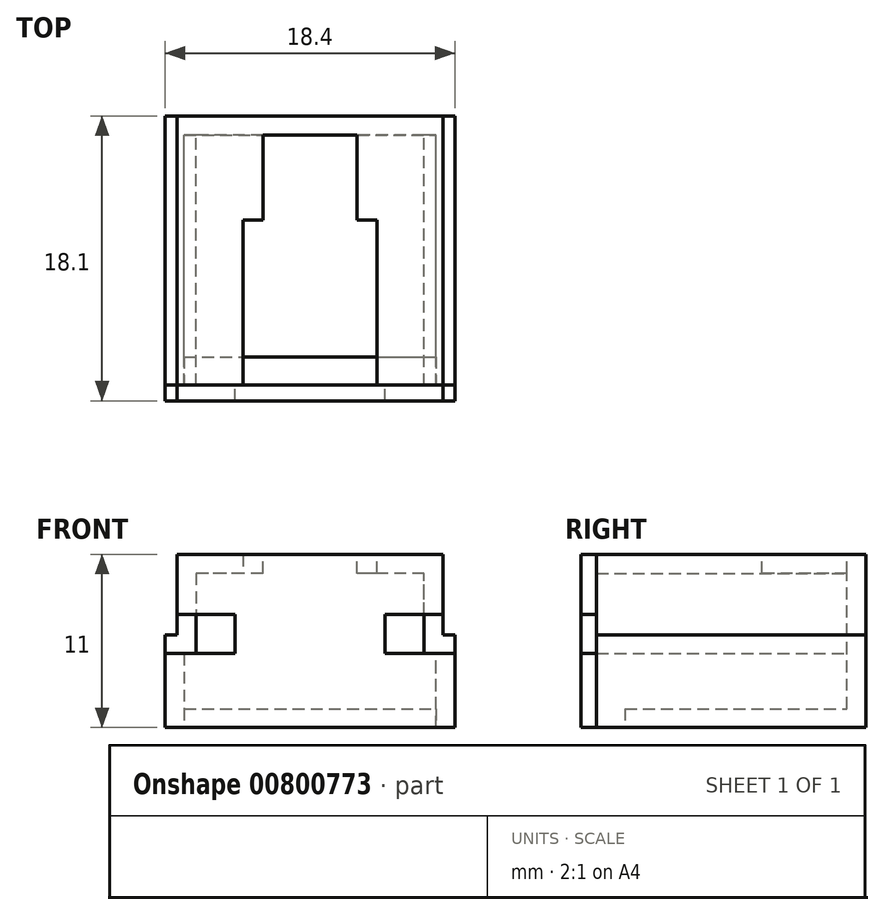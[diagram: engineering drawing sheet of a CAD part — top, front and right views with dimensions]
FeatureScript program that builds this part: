
annotation { "Feature Type Name" : "Feature", "Feature Type Description" : "" }
export const myFeature = defineFeature(function(context is Context, id is Id, definition is map)
    precondition{}
    {
        {
            var Q0;
            Q0=qCreatedBy(makeId("Front.planeOp"),FACE);
            var sketch = newSketch(context, id + "F0", { "sketchPlane" : qUnion([Q0])});
            skLineSegment(sketch, "E0", {"start": v(-9.2, 0) * mm, "end": v(9.2, 0) * mm});
            skLineSegment(sketch, "E1", {"start": v(-8.45, 11) * mm, "end": v(-4.25, 11) * mm});
            skLineSegment(sketch, "E2", {"start": v(-4.25, 11) * mm, "end": v(-4.25, 9.8) * mm});
            skLineSegment(sketch, "E3", {"start": v(-4.25, 9.8) * mm, "end": v(-7.25, 9.8) * mm});
            skLineSegment(sketch, "E4", {"start": v(-7.25, 9.8) * mm, "end": v(-7.25, 4.7) * mm});
            skLineSegment(sketch, "E5", {"start": v(-7.25, 4.7) * mm, "end": v(-8, 4.7) * mm});
            skLineSegment(sketch, "E6", {"start": v(-8, 4.7) * mm, "end": v(-8, 1.2) * mm});
            skLineSegment(sketch, "E7", {"start": v(-8, 1.2) * mm, "end": v(8, 1.2) * mm});
            skLineSegment(sketch, "E8", {"start": v(8, 1.2) * mm, "end": v(8, 4.7) * mm});
            skLineSegment(sketch, "E9", {"start": v(8, 4.7) * mm, "end": v(7.25, 4.7) * mm});
            skLineSegment(sketch, "E10", {"start": v(7.25, 4.7) * mm, "end": v(7.25, 9.8) * mm});
            skLineSegment(sketch, "E11", {"start": v(7.25, 9.8) * mm, "end": v(4.25, 9.8) * mm});
            skLineSegment(sketch, "E12", {"start": v(4.25, 9.8) * mm, "end": v(4.25, 11) * mm});
            skLineSegment(sketch, "E13", {"start": v(4.25, 11) * mm, "end": v(8.45, 11) * mm});
            skLineSegment(sketch, "E14", {"start": v(4.25, 11) * mm, "end": v(-4.25, 11) * mm, "construction": true});
            skLineSegment(sketch, "E15", {"start": v(0, 0) * mm, "end": v(0, 11) * mm, "construction": true});
            skLineSegment(sketch, "E16.bottom", {"start": v(4.25, 9.8) * mm, "end": v(3, 9.8) * mm});
            skLineSegment(sketch, "E16.top", {"start": v(4.25, 11) * mm, "end": v(3, 11) * mm});
            skLineSegment(sketch, "E16.right", {"start": v(3, 9.8) * mm, "end": v(3, 11) * mm});
            skLineSegment(sketch, "E17.bottom", {"start": v(-4.25, 9.8) * mm, "end": v(-3, 9.8) * mm});
            skLineSegment(sketch, "E17.top", {"start": v(-4.25, 11) * mm, "end": v(-3, 11) * mm});
            skLineSegment(sketch, "E17.left", {"start": v(-4.25, 9.8) * mm, "end": v(-4.25, 11) * mm});
            skLineSegment(sketch, "E17.right", {"start": v(-3, 9.8) * mm, "end": v(-3, 11) * mm});
            skLineSegment(sketch, "E18", {"start": v(-9.2, 0) * mm, "end": v(-9.2, 5.9) * mm});
            skLineSegment(sketch, "E19", {"start": v(-9.2, 5.9) * mm, "end": v(-8.45, 5.9) * mm});
            skLineSegment(sketch, "E20", {"start": v(-8.45, 5.9) * mm, "end": v(-8.45, 11) * mm});
            skLineSegment(sketch, "E21", {"start": v(9.2, 0) * mm, "end": v(9.2, 5.9) * mm});
            skLineSegment(sketch, "E22", {"start": v(9.2, 5.9) * mm, "end": v(8.45, 5.9) * mm});
            skLineSegment(sketch, "E23", {"start": v(8.45, 5.9) * mm, "end": v(8.45, 11) * mm});
            skSolve(sketch);
        }
        {
            var Q0;
            Q0=makeQuery(id+"F0.imprint","IMPRINT",FACE,{"disambiguationData":[TD([[makeQuery(id+"F0.imprint","IMPRINT",EDGE,{"derivedFrom":sQuery(id+"F0.wireOp",EDGE,"E0")}),1.0]])]});
            extrude(context, id + "F1", {"entities" : qUnion([Q0]), "depth" : 10.5 * mm, "offsetDistance" : 25 * mm});
        }
        {
            var Q0;
            Q0=makeQuery(id+"F0.imprint","IMPRINT",FACE,{"disambiguationData":[TD([[makeQuery(id+"F0.imprint","IMPRINT",EDGE,{"derivedFrom":sQuery(id+"F0.wireOp",EDGE,"E16.bottom")}),-1.0]])]});
            var Q1;
            Q1=makeQuery(id+"F0.imprint","IMPRINT",FACE,{"disambiguationData":[TD([[makeQuery(id+"F0.imprint","IMPRINT",EDGE,{"derivedFrom":sQuery(id+"F0.wireOp",EDGE,"E0")}),1.0]])]});
            var Q2;
            Q2=makeQuery(id+"F0.imprint","IMPRINT",FACE,{"disambiguationData":[TD([[makeQuery(id+"F0.imprint","IMPRINT",EDGE,{"derivedFrom":sQuery(id+"F0.wireOp",EDGE,"E17.bottom")}),1.0]])]});
            extrude(context, id + "F2", {"entities" : qUnion([Q0, Q1, Q2]), "operationType" : NewBodyOperationType.ADD, "oppositeDirection" : true, "depth" : 5.4 * mm, "offsetDistance" : 25 * mm});
        }
        {
            var Q0;
            Q0=makeQuery(id+"F2.opExtrude","CAP_FACE",FACE,{"disambiguationData":[OSD([sQuery(id+"F0.wireOp",EDGE,"E0"),sQuery(id+"F0.wireOp",EDGE,"EI1BiXlL-Q3jm-eNfy-wKam-WfHQaEUP30CD"),sQuery(id+"F0.wireOp",EDGE,"E1"),sQuery(id+"F0.wireOp",EDGE,"E3"),sQuery(id+"F0.wireOp",EDGE,"E4"),sQuery(id+"F0.wireOp",EDGE,"E5"),sQuery(id+"F0.wireOp",EDGE,"E6"),sQuery(id+"F0.wireOp",EDGE,"E7"),sQuery(id+"F0.wireOp",EDGE,"E8"),sQuery(id+"F0.wireOp",EDGE,"E9"),sQuery(id+"F0.wireOp",EDGE,"E10"),sQuery(id+"F0.wireOp",EDGE,"E11"),sQuery(id+"F0.wireOp",EDGE,"E13"),sQuery(id+"F0.wireOp",EDGE,"ufck05Tf-Zb9H-2oP1-nLNF-ijk2fNiCipJR"),sQuery(id+"F0.wireOp",EDGE,"E16.bottom"),sQuery(id+"F0.wireOp",EDGE,"E16.top"),sQuery(id+"F0.wireOp",EDGE,"E16.right"),sQuery(id+"F0.wireOp",EDGE,"E17.bottom"),sQuery(id+"F0.wireOp",EDGE,"E17.top"),sQuery(id+"F0.wireOp",EDGE,"E17.right")])],"isStart":false});
            var sketch = newSketch(context, id + "F3", { "sketchPlane" : qUnion([Q0])});
            skLineSegment(sketch, "E24.0.3", {"start": v(-8.45, 11) * mm, "end": v(-8.45, 5.9) * mm});
            skLineSegment(sketch, "E24.0.4", {"start": v(-8.45, 5.9) * mm, "end": v(-9.2, 5.9) * mm});
            skLineSegment(sketch, "E24.0.5", {"start": v(-9.2, 5.9) * mm, "end": v(-9.2, 0) * mm});
            skLineSegment(sketch, "E24.0.6", {"start": v(-9.2, 0) * mm, "end": v(9.2, 0) * mm});
            skLineSegment(sketch, "E24.0.7", {"start": v(9.2, 0) * mm, "end": v(9.2, 5.9) * mm});
            skLineSegment(sketch, "E24.0.8", {"start": v(9.2, 5.9) * mm, "end": v(8.45, 5.9) * mm});
            skLineSegment(sketch, "E24.0.9", {"start": v(8.45, 5.9) * mm, "end": v(8.45, 11) * mm});
            skLineSegment(sketch, "E25", {"start": v(-8.45, 11) * mm, "end": v(8.45, 11) * mm});
            skSolve(sketch);
        }
        {
            var Q0;
            Q0 = qSketchRegion(id + "F3", true);
            extrude(context, id + "F4", {"entities" : qUnion([Q0]), "operationType" : NewBodyOperationType.ADD, "depth" : 1.2 * mm, "offsetDistance" : 25 * mm});
        }
        {
            var Q0;
            Q0=makeQuery(id+"F1.opExtrude","CAP_FACE",FACE,{"disambiguationData":[OSD([sQuery(id+"F0.wireOp",EDGE,"E0"),sQuery(id+"F0.wireOp",EDGE,"E1"),sQuery(id+"F0.wireOp",EDGE,"E3"),sQuery(id+"F0.wireOp",EDGE,"E4"),sQuery(id+"F0.wireOp",EDGE,"E5"),sQuery(id+"F0.wireOp",EDGE,"E6"),sQuery(id+"F0.wireOp",EDGE,"E7"),sQuery(id+"F0.wireOp",EDGE,"E8"),sQuery(id+"F0.wireOp",EDGE,"E9"),sQuery(id+"F0.wireOp",EDGE,"E10"),sQuery(id+"F0.wireOp",EDGE,"E11"),sQuery(id+"F0.wireOp",EDGE,"E13"),sQuery(id+"F0.wireOp",EDGE,"E12"),sQuery(id+"F0.wireOp",EDGE,"E17.left"),sQuery(id+"F0.wireOp",EDGE,"E18"),sQuery(id+"F0.wireOp",EDGE,"E19"),sQuery(id+"F0.wireOp",EDGE,"E20"),sQuery(id+"F0.wireOp",EDGE,"E21"),sQuery(id+"F0.wireOp",EDGE,"E22"),sQuery(id+"F0.wireOp",EDGE,"E23")])],"isStart":false});
            var sketch = newSketch(context, id + "F5", { "sketchPlane" : qUnion([Q0])});
            skLineSegment(sketch, "E26", {"start": v(-8, 1.2) * mm, "end": v(-8, 0) * mm});
            skLineSegment(sketch, "E27", {"start": v(8, 1.2) * mm, "end": v(8, 0) * mm});
            skLineSegment(sketch, "E28", {"start": v(-8, 1.2) * mm, "end": v(8, 1.2) * mm});
            skLineSegment(sketch, "E29", {"start": v(8, 0) * mm, "end": v(-8, 0) * mm});
            skSolve(sketch);
        }
        {
            var Q0;
            Q0 = qSketchRegion(id + "F5", true);
            extrude(context, id + "F6", {"entities" : qUnion([Q0]), "operationType" : NewBodyOperationType.REMOVE, "oppositeDirection" : true, "depth" : 1.8 * mm, "offsetDistance" : 25 * mm});
        }
        {
            var Q0;
            {var subQ0=sQuery(id+"F0.wireOp",EDGE,"E18");var subQ1=sQuery(id+"F0.wireOp",EDGE,"E13");var subQ2=sQuery(id+"F0.wireOp",EDGE,"E4");var subQ3=sQuery(id+"F0.wireOp",EDGE,"E1");var subQ4=sQuery(id+"F0.wireOp",EDGE,"E0");var subQ5=sQuery(id+"F0.wireOp",EDGE,"E20");var subQ6=sQuery(id+"F0.wireOp",EDGE,"E3");var subQ7=sQuery(id+"F0.wireOp",EDGE,"E5");var subQ8=sQuery(id+"F0.wireOp",EDGE,"E17.left");var subQ9=sQuery(id+"F0.wireOp",EDGE,"E19");var subQ10=sQuery(id+"F0.wireOp",EDGE,"E6");Q0=makeQuery(id+"F6.boolean.opBoolean","SPLIT",FACE,{"disambiguationData":[TD([makeQuery(id+"F1.opExtrude","SWEPT_FACE",FACE,{"disambiguationData":[OSD([subQ6])]})])],"derivedFrom":makeQuery(id+"F1.opExtrude","CAP_FACE",FACE,{"disambiguationData":[OSD([subQ4,subQ3,subQ6,subQ2,subQ7,subQ10,sQuery(id+"F0.wireOp",EDGE,"E7"),sQuery(id+"F0.wireOp",EDGE,"E8"),sQuery(id+"F0.wireOp",EDGE,"E9"),sQuery(id+"F0.wireOp",EDGE,"E10"),sQuery(id+"F0.wireOp",EDGE,"E11"),subQ1,sQuery(id+"F0.wireOp",EDGE,"E12"),subQ8,subQ0,subQ9,subQ5,sQuery(id+"F0.wireOp",EDGE,"E21"),sQuery(id+"F0.wireOp",EDGE,"E22"),sQuery(id+"F0.wireOp",EDGE,"E23")])],"isStart":false})});}
            var sketch = newSketch(context, id + "F7", { "sketchPlane" : qUnion([Q0])});
            skLineSegment(sketch, "E30.0", {"start": v(8.45, 7.2) * mm, "end": v(8.45, 11) * mm});
            skLineSegment(sketch, "E30.1", {"start": v(9.2, 0) * mm, "end": v(9.2, 4.7) * mm});
            skLineSegment(sketch, "E30.3", {"start": v(-8.45, 7.2) * mm, "end": v(-8.45, 11) * mm});
            skLineSegment(sketch, "E30.5", {"start": v(-9.2, 0) * mm, "end": v(-9.2, 4.7) * mm});
            skLineSegment(sketch, "E31", {"start": v(-8.45, 11) * mm, "end": v(8.45, 11) * mm});
            skLineSegment(sketch, "E32", {"start": v(9.2, 0) * mm, "end": v(-9.2, 0) * mm});
            skLineSegment(sketch, "E33", {"start": v(-8.45, 7.2) * mm, "end": v(-4.75, 7.2) * mm});
            skLineSegment(sketch, "E34", {"start": v(-4.75, 7.2) * mm, "end": v(-4.75, 4.7) * mm});
            skLineSegment(sketch, "E35", {"start": v(-4.75, 4.7) * mm, "end": v(-9.2, 4.7) * mm});
            skLineSegment(sketch, "E36", {"start": v(8.45, 7.2) * mm, "end": v(4.75, 7.2) * mm});
            skLineSegment(sketch, "E37", {"start": v(4.75, 7.2) * mm, "end": v(4.75, 4.7) * mm});
            skLineSegment(sketch, "E38", {"start": v(4.75, 4.7) * mm, "end": v(9.2, 4.7) * mm});
            skSolve(sketch);
        }
        {
            var Q0;
            Q0 = qSketchRegion(id + "F7", true);
            extrude(context, id + "F8", {"entities" : qUnion([Q0]), "depth" : 1 * mm, "offsetDistance" : 25 * mm});
        }
    });
